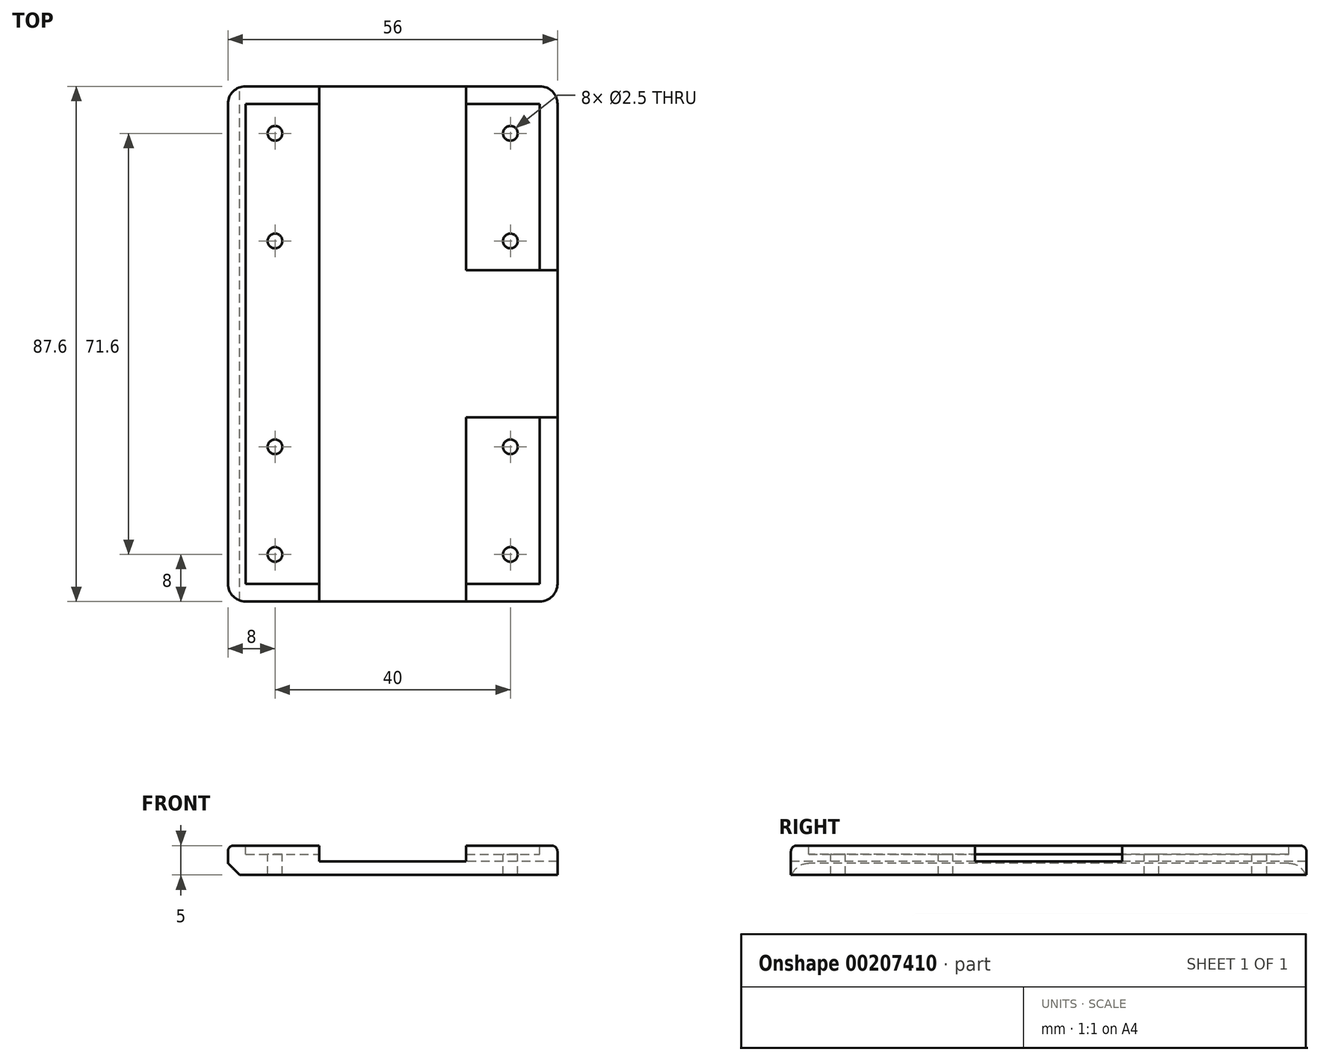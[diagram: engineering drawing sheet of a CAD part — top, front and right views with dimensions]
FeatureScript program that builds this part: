
annotation { "Feature Type Name" : "Feature", "Feature Type Description" : "" }
export const myFeature = defineFeature(function(context is Context, id is Id, definition is map)
    precondition{}
    {
        {
            var Q0;
            Q0=qCreatedBy(makeId("Top.planeOp"),FACE);
            var sketch = newSketch(context, id + "F0", { "sketchPlane" : qUnion([Q0])});
            skLineSegment(sketch, "E0.bottom", {"start": v(28, -43.8) * mm, "end": v(-28, -43.8) * mm});
            skLineSegment(sketch, "E0.top", {"start": v(28, 43.8) * mm, "end": v(-28, 43.8) * mm});
            skLineSegment(sketch, "E0.left", {"start": v(28, -43.8) * mm, "end": v(28, 43.8) * mm});
            skLineSegment(sketch, "E0.right", {"start": v(-28, -43.8) * mm, "end": v(-28, 43.8) * mm});
            skPoint(sketch, "E0.middle", {"position": v(0, 0) * mm});
            skSolve(sketch);
        }
        {
            var Q0;
            Q0=makeQuery(id+"F0.imprint","IMPRINT",FACE,{"disambiguationData":[TD([[makeQuery(id+"F0.imprint","IMPRINT",EDGE,{"derivedFrom":sQuery(id+"F0.wireOp",EDGE,"E0.bottom")}),-1.0]])]});
            extrude(context, id + "F1", {"entities" : qUnion([Q0]), "depth" : 5 * mm});
        }
        {
            var Q0;
            Q0=makeQuery(id+"F1.opExtrude","CAP_FACE",FACE,{"disambiguationData":[OSD([sQuery(id+"F0.wireOp",EDGE,"E0.bottom"),sQuery(id+"F0.wireOp",EDGE,"E0.top"),sQuery(id+"F0.wireOp",EDGE,"E0.left"),sQuery(id+"F0.wireOp",EDGE,"E0.right")])],"isStart":false});
            var sketch = newSketch(context, id + "F11", { "sketchPlane" : qUnion([Q0])});
            skCircle(sketch, "E1", {"center": v(28, 28.8) * mm, "radius": 10 * mm});
            skSolve(sketch);
        }
        {
            var Q0;
            Q0=makeQuery(id+"F1.opExtrude","CAP_EDGE",EDGE,{"disambiguationData":[OSD([sQuery(id+"F0.wireOp",EDGE,"E0.right")])],"isStart":true});
            chamfer(context, id + "F2", {"entities" : qUnion([Q0]), "width" : 2 * mm, "tangentPropagation" : true});
        }
        {
            var Q0;
            Q0=makeQuery(id+"F1.opExtrude","CAP_FACE",FACE,{"disambiguationData":[OSD([sQuery(id+"F0.wireOp",EDGE,"E0.bottom"),sQuery(id+"F0.wireOp",EDGE,"E0.top"),sQuery(id+"F0.wireOp",EDGE,"E0.left"),sQuery(id+"F0.wireOp",EDGE,"E0.right")])],"isStart":false});
            var sketch = newSketch(context, id + "F3", { "sketchPlane" : qUnion([Q0])});
            skLineSegment(sketch, "E2", {"start": v(-12.5, 43.8) * mm, "end": v(-12.5, -43.8) * mm});
            skLineSegment(sketch, "E3", {"start": v(12.5, 43.8) * mm, "end": v(12.5, -43.8) * mm});
            skLineSegment(sketch, "E4", {"start": v(-12.5, 43.8) * mm, "end": v(12.5, 43.8) * mm});
            skLineSegment(sketch, "E5", {"start": v(12.5, -43.8) * mm, "end": v(-12.5, -43.8) * mm});
            skLineSegment(sketch, "E6", {"start": v(12.5, 12.5) * mm, "end": v(28, 12.5) * mm});
            skLineSegment(sketch, "E7", {"start": v(28, 12.5) * mm, "end": v(28, -12.5) * mm});
            skLineSegment(sketch, "E8", {"start": v(28, -12.5) * mm, "end": v(12.5, -12.5) * mm});
            skPoint(sketch, "E9", {"position": v(0, 43.8) * mm});
            skPoint(sketch, "E10", {"position": v(28, 0) * mm});
            skSolve(sketch);
        }
        {
            var Q0;
            Q0=makeQuery(id+"F3.imprint","IMPRINT",FACE,{"disambiguationData":[TD([[makeQuery(id+"F3.imprint","IMPRINT",EDGE,{"derivedFrom":sQuery(id+"F3.wireOp",EDGE,"E2")}),1.0]])]});
            var Q1;
            {var subQ0=sQuery(id+"F3.wireOp",EDGE,"E6");Q1=makeQuery(id+"F3.imprint","IMPRINT",FACE,{"disambiguationData":[TD([[makeQuery(id+"F3.imprint","IMPRINT",EDGE,{"derivedFrom":subQ0}),-1.0]])]});}
            extrude(context, id + "F4", {"entities" : qUnion([Q0, Q1]), "operationType" : NewBodyOperationType.REMOVE, "oppositeDirection" : true, "depth" : 2.7 * mm});
        }
        {
            var Q0;
            Q0=makeQuery(id+"F1.opExtrude","SWEPT_EDGE",EDGE,{"disambiguationData":[OSD([sQuery(id+"F0.wireOp",EDGE,"E0.top"),sQuery(id+"F0.wireOp",EDGE,"E0.right")])]});
            var Q1;
            Q1=makeQuery(id+"F1.opExtrude","SWEPT_EDGE",EDGE,{"disambiguationData":[OSD([sQuery(id+"F0.wireOp",EDGE,"E0.bottom"),sQuery(id+"F0.wireOp",EDGE,"E0.right")])]});
            var Q2;
            Q2=makeQuery(id+"F1.opExtrude","SWEPT_EDGE",EDGE,{"disambiguationData":[OSD([sQuery(id+"F0.wireOp",EDGE,"E0.bottom"),sQuery(id+"F0.wireOp",EDGE,"E0.left")])]});
            var Q3;
            Q3=makeQuery(id+"F1.opExtrude","SWEPT_EDGE",EDGE,{"disambiguationData":[OSD([sQuery(id+"F0.wireOp",EDGE,"E0.top"),sQuery(id+"F0.wireOp",EDGE,"E0.left")])]});
            fillet(context, id + "F5", {"entities" : qUnion([Q0, Q1, Q2, Q3]), "radius" : 3 * mm, "tangentPropagation" : true, "allowEdgeOverflow" : false});
        }
        {
            var Q0;
            {var subQ0=sQuery(id+"F0.wireOp",EDGE,"E0.bottom");var subQ1=sQuery(id+"F0.wireOp",EDGE,"E0.top");var subQ2=sQuery(id+"F0.wireOp",EDGE,"E0.right");Q0=makeQuery(id+"F4.boolean.opBoolean","SPLIT",FACE,{"disambiguationData":[TD([makeQuery(id+"F1.opExtrude","SWEPT_FACE",FACE,{"disambiguationData":[OSD([subQ2])]})])],"derivedFrom":makeQuery(id+"F1.opExtrude","CAP_FACE",FACE,{"disambiguationData":[OSD([subQ0,subQ1,sQuery(id+"F0.wireOp",EDGE,"E0.left"),subQ2])],"isStart":false})});}
            cPlane(context, id + "F6", {"entities" : qUnion([Q0]), "cplaneType" : CPlaneType.OFFSET, "offset" : 0 * mm, "width" : 150 * mm, "height" : 150 * mm});
        }
        {
            var Q0;
            Q0=qCreatedBy(id+"F6.planeOp",FACE);
            var sketch = newSketch(context, id + "F7", { "sketchPlane" : qUnion([Q0])});
            skLineSegment(sketch, "E11.0", {"start": v(-12.5, 43.8) * mm, "end": v(-25, 43.8) * mm, "construction": true});
            skLineSegment(sketch, "E12.0", {"start": v(-28, -40.8) * mm, "end": v(-28, 40.8) * mm, "construction": true});
            skLineSegment(sketch, "E13.0", {"start": v(25, 43.8) * mm, "end": v(12.5, 43.8) * mm, "construction": true});
            skLineSegment(sketch, "E14.0", {"start": v(28, 12.5) * mm, "end": v(28, 40.8) * mm, "construction": true});
            skPoint(sketch, "E15.0", {"position": v(18.75, -43.8) * mm});
            skLineSegment(sketch, "E16.0", {"start": v(25, -43.8) * mm, "end": v(12.5, -43.8) * mm});
            skLineSegment(sketch, "E17.0", {"start": v(28, -40.8) * mm, "end": v(28, -12.5) * mm});
            skLineSegment(sketch, "E18.bottom", {"start": v(-25, 40.8) * mm, "end": v(25, 40.8) * mm});
            skLineSegment(sketch, "E18.top", {"start": v(-25, -40.8) * mm, "end": v(25, -40.8) * mm});
            skLineSegment(sketch, "E18.left", {"start": v(-25, 40.8) * mm, "end": v(-25, -40.8) * mm});
            skLineSegment(sketch, "E18.right", {"start": v(25, 40.8) * mm, "end": v(25, -40.8) * mm});
            skPoint(sketch, "E19", {"position": v(-20, -35.8) * mm});
            skPoint(sketch, "E20", {"position": v(20, -35.8) * mm});
            skPoint(sketch, "E21", {"position": v(20, -17.5) * mm});
            skPoint(sketch, "E22", {"position": v(20, 17.5) * mm});
            skPoint(sketch, "E23", {"position": v(20, 35.8) * mm});
            skPoint(sketch, "E24", {"position": v(-20, 35.8) * mm});
            skPoint(sketch, "E25", {"position": v(-20, 17.5) * mm});
            skPoint(sketch, "E26", {"position": v(-20, -17.5) * mm});
            skSolve(sketch);
        }
        {
            var Q0;
            Q0=makeQuery(id+"F7.imprint","IMPRINT",FACE,{"disambiguationData":[TD([[makeQuery(id+"F7.imprint","IMPRINT",EDGE,{"derivedFrom":sQuery(id+"F7.wireOp",EDGE,"E18.bottom")}),-1.0]])]});
            extrude(context, id + "F8", {"entities" : qUnion([Q0]), "operationType" : NewBodyOperationType.REMOVE, "oppositeDirection" : true, "depth" : 1.5 * mm});
        }
        {
            var Q0;
            {var subQ0=sQuery(id+"F0.wireOp",EDGE,"E0.bottom");var subQ1=sQuery(id+"F0.wireOp",EDGE,"E0.top");var subQ2=sQuery(id+"F0.wireOp",EDGE,"E0.right");Q0=makeQuery(id+"F5.opFillet","BLEND_EDGE",EDGE,{"blendedFrom":[makeQuery(id+"F1.opExtrude","SWEPT_EDGE",EDGE,{"disambiguationData":[OSD([subQ1,subQ2])]}),makeQuery(id+"F4.boolean.opBoolean","SPLIT",FACE,{"disambiguationData":[TD([makeQuery(id+"F1.opExtrude","SWEPT_FACE",FACE,{"disambiguationData":[OSD([subQ2])]})])],"derivedFrom":makeQuery(id+"F1.opExtrude","CAP_FACE",FACE,{"disambiguationData":[OSD([subQ0,subQ1,sQuery(id+"F0.wireOp",EDGE,"E0.left"),subQ2])],"isStart":false})})],"blendedInto":[makeQuery(id+"F4.boolean.opBoolean","SPLIT",FACE,{"disambiguationData":[TD([makeQuery(id+"F1.opExtrude","SWEPT_FACE",FACE,{"disambiguationData":[OSD([subQ2])]})])],"derivedFrom":makeQuery(id+"F1.opExtrude","CAP_FACE",FACE,{"disambiguationData":[OSD([subQ0,subQ1,sQuery(id+"F0.wireOp",EDGE,"E0.left"),subQ2])],"isStart":false})})]});}
            var Q1;
            {var subQ0=sQuery(id+"F0.wireOp",EDGE,"E0.top");var subQ2=sQuery(id+"F3.wireOp",EDGE,"E6");var subQ3=sQuery(id+"F0.wireOp",EDGE,"E0.left");Q1=makeQuery(id+"F5.opFillet","BLEND_EDGE",EDGE,{"blendedFrom":[makeQuery(id+"F1.opExtrude","SWEPT_EDGE",EDGE,{"disambiguationData":[OSD([subQ0,subQ3])]}),makeQuery(id+"F4.boolean.opBoolean","SPLIT",FACE,{"disambiguationData":[TD([makeQuery(id+"F4.opExtrude","SWEPT_FACE",FACE,{"disambiguationData":[OSD([subQ2])]})])],"derivedFrom":makeQuery(id+"F1.opExtrude","CAP_FACE",FACE,{"disambiguationData":[OSD([sQuery(id+"F0.wireOp",EDGE,"E0.bottom"),subQ0,subQ3,sQuery(id+"F0.wireOp",EDGE,"E0.right")])],"isStart":false})})],"blendedInto":[makeQuery(id+"F4.boolean.opBoolean","SPLIT",FACE,{"disambiguationData":[TD([makeQuery(id+"F4.opExtrude","SWEPT_FACE",FACE,{"disambiguationData":[OSD([subQ2])]})])],"derivedFrom":makeQuery(id+"F1.opExtrude","CAP_FACE",FACE,{"disambiguationData":[OSD([sQuery(id+"F0.wireOp",EDGE,"E0.bottom"),subQ0,subQ3,sQuery(id+"F0.wireOp",EDGE,"E0.right")])],"isStart":false})})]});}
            var Q2;
            {var subQ0=sQuery(id+"F0.wireOp",EDGE,"E0.left");var subQ1=sQuery(id+"F0.wireOp",EDGE,"E0.top");var subQ3=makeQuery(id+"F1.opExtrude","CAP_EDGE",EDGE,{"disambiguationData":[OSD([subQ1])],"isStart":false});Q2=makeQuery(id+"F4.boolean.opBoolean","SPLIT",EDGE,{"disambiguationData":[TD([makeQuery(id+"F1.opExtrude","SWEPT_FACE",FACE,{"disambiguationData":[OSD([subQ0])]})])],"derivedFrom":subQ3});}
            var Q3;
            {var subQ0=sQuery(id+"F0.wireOp",EDGE,"E0.right");var subQ1=sQuery(id+"F0.wireOp",EDGE,"E0.top");Q3=makeQuery(id+"F4.boolean.opBoolean","SPLIT",EDGE,{"disambiguationData":[TD([makeQuery(id+"F1.opExtrude","SWEPT_FACE",FACE,{"disambiguationData":[OSD([subQ0])]})])],"derivedFrom":makeQuery(id+"F1.opExtrude","CAP_EDGE",EDGE,{"disambiguationData":[OSD([subQ1])],"isStart":false})});}
            var Q4;
            Q4=makeQuery(id+"F1.opExtrude","CAP_EDGE",EDGE,{"disambiguationData":[OSD([sQuery(id+"F0.wireOp",EDGE,"E0.right")])],"isStart":false});
            var Q5;
            {var subQ0=sQuery(id+"F0.wireOp",EDGE,"E0.bottom");var subQ1=sQuery(id+"F0.wireOp",EDGE,"E0.right");Q5=makeQuery(id+"F4.boolean.opBoolean","SPLIT",EDGE,{"disambiguationData":[TD([makeQuery(id+"F1.opExtrude","SWEPT_FACE",FACE,{"disambiguationData":[OSD([subQ1])]})])],"derivedFrom":makeQuery(id+"F1.opExtrude","CAP_EDGE",EDGE,{"disambiguationData":[OSD([subQ0])],"isStart":false})});}
            var Q6;
            {var subQ0=sQuery(id+"F0.wireOp",EDGE,"E0.bottom");var subQ1=sQuery(id+"F0.wireOp",EDGE,"E0.left");var subQ3=sQuery(id+"F3.wireOp",EDGE,"E8");Q6=makeQuery(id+"F5.opFillet","BLEND_EDGE",EDGE,{"blendedFrom":[makeQuery(id+"F1.opExtrude","SWEPT_EDGE",EDGE,{"disambiguationData":[OSD([subQ0,subQ1])]}),makeQuery(id+"F4.boolean.opBoolean","SPLIT",FACE,{"disambiguationData":[TD([makeQuery(id+"F4.opExtrude","SWEPT_FACE",FACE,{"disambiguationData":[OSD([subQ3])]})])],"derivedFrom":makeQuery(id+"F1.opExtrude","CAP_FACE",FACE,{"disambiguationData":[OSD([subQ0,sQuery(id+"F0.wireOp",EDGE,"E0.top"),subQ1,sQuery(id+"F0.wireOp",EDGE,"E0.right")])],"isStart":false})})],"blendedInto":[makeQuery(id+"F4.boolean.opBoolean","SPLIT",FACE,{"disambiguationData":[TD([makeQuery(id+"F4.opExtrude","SWEPT_FACE",FACE,{"disambiguationData":[OSD([subQ3])]})])],"derivedFrom":makeQuery(id+"F1.opExtrude","CAP_FACE",FACE,{"disambiguationData":[OSD([subQ0,sQuery(id+"F0.wireOp",EDGE,"E0.top"),subQ1,sQuery(id+"F0.wireOp",EDGE,"E0.right")])],"isStart":false})})]});}
            fillet(context, id + "F9", {"entities" : qUnion([Q0, Q1, Q2, Q3, Q4, Q5, Q6]), "radius" : 1 * mm, "tangentPropagation" : true, "allowEdgeOverflow" : false});
        }
        {
            var Q0;
            Q0=sQuery(id+"F7.wireOp",VERTEX,"E24");
            var Q1;
            Q1=sQuery(id+"F7.wireOp",VERTEX,"E23");
            var Q2;
            Q2=sQuery(id+"F7.wireOp",VERTEX,"E22");
            var Q3;
            Q3=sQuery(id+"F7.wireOp",VERTEX,"E21");
            var Q4;
            Q4=sQuery(id+"F7.wireOp",VERTEX,"E20");
            var Q5;
            Q5=sQuery(id+"F7.wireOp",VERTEX,"E19");
            var Q6;
            Q6=sQuery(id+"F7.wireOp",VERTEX,"E25");
            var Q7;
            Q7=sQuery(id+"F7.wireOp",VERTEX,"E26");
            var Q8;
            Q8=makeQuery(id+"F1.opExtrude","SWEPT_BODY",BODY,{"disambiguationData":[OSD([sQuery(id+"F0.wireOp",EDGE,"E0.bottom"),sQuery(id+"F0.wireOp",EDGE,"E0.top"),sQuery(id+"F0.wireOp",EDGE,"E0.left"),sQuery(id+"F0.wireOp",EDGE,"E0.right")])]});
            hole(context, id + "F10", {"style" : HoleStyle.SIMPLE, "endStyle" : HoleEndStyle.BLIND, "holeDiameter" : 2.5 * mm, "holeDepth" : 68 * mm, "locations" : qUnion([Q0, Q1, Q2, Q3, Q4, Q5, Q6, Q7]), "scope" : qUnion([Q8])});
        }
    });
